# Revit family: Seating-Casual-Naughtone-Viv_WD_CnterHght_Stool2
name_source: partatom
category: Furniture
revit_build: Autodesk Revit 2015 (Build: 20150704_0715(x64)
units: mm (PartAtom-declared; Revit-internal decimal feet)

## types (1)
- 560mmx560mmx910mm
    Additional Materials = Additional material and finish options available. Please contact Naughtone direct for further information.
    Assembly Code = E2020200
    AssetIdentifier = VIV-CBS-WD
    AssetType = Movable
    BIMObjectName = Seating-Casual-Naughtone-Viv_WD_CnterHght_Stool
    BarCode = 0.000000
    Base Options = Chromed mild steel base as standard. White powder coated steel frame and other RAL colours available on request. Please contact Naughtone direct for further information.
    Category = 40.50.12.85 : Stools
    CodePerformance = FISP Certified; ISO14001 Certified
    Color = Royal Blue
    ComponentDescription = Simple and very comfortable, the Viv chair's paired down shape is highlighted by its tight upholstery, cleverly held deeply into the bucket seat.
    Constituents = CMHR Foam; Formed Plywood; Fabric; Wood
    Cost = 0 $
    Description = Viv Wood Counter Height Stool
    DurationUnit = Years
    ExpectedLife = 15-20
    Finish = Fabric
    Grade = 3
    Keynote = 40.50.12.85
    Manufacturer = Naughtone
    ManufacturerDetailsUK = 201 Pannal Business Park, Station Road, Harrogate, HG3 1JL
    Material = Fabric; Wood Frame
    Model = VIV-CBS-WD
    ModelNumber = VIV-CBS-WD
    ModelReference = Viv Wood Counter Height Stool
    Mtrl_Footrest = Plastic-Gen-Black
    NBSReference = 40.50.12.85
    Name = Seating-Casual-Naughtone-Viv_WD_CnterHght_Stool
    NominalHeight = 910 mm
    NominalLength = 560 mm  [stored 1.83727 ft]
    NominalWidth = 560 mm  [stored 1.83727 ft]
    Option = Wood Base
    Product URL = http://www.naughtone.com
    ProductInformation = http://www.naughtone.com
    ReplacementCost = 0.00
    SeatHeight = 660 mm
    SerialNumber = 0.000000
    Shape = Organic
    Size = 560mmx560mmx910mm
    SustainabilityPerformance = 75.6% Compostable (base & plywood frame)
    TagNumber = 0.000000
    Type Comments = 560x560x910
    TypeName = 560mmx560mmx910mm, Viv Wood Counter Height Stool
    URL = http://www.naughtone.com
    Uniclass2015 = 40.50.12.85
    Version = 1
    WarrantyDescription = 5 Year Warranty
    WarrantyDurationLabor = 5
    WarrantyDurationParts = 5
    WarrantyDurationUnit = Years
    _BIMspec_GUID = 0
    _current revision = 1
    _distributed by = www.bimbox.co.uk

note: [stored X ft] marks values corroborated as IEEE doubles in the binary element streams (Revit-internal decimal feet)

## geometry (parser evidence)
native form markers: Sweep x3
no freeform markers — native parametric forms only
